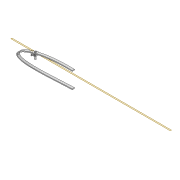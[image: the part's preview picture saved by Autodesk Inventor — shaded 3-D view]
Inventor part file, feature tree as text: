
AUTODESK INVENTOR PART (.ipt)
format: ipt  version: 2022 (Build 260153000, 153)  size: 545,280 bytes
history: native  units: mm
features: extrude x9, sketch x9, projected_geometry x7, plane x4, shell x1, fillet x1
ambient origin geometry x8: Origin, YZ Plane, XZ Plane, XY Plane, X Axis, Y Axis, Z Axis, Center Point
bodies: Solid1 (feature_tree)
feature tree (31):
  extrude  "Extrusion1"  Depth=3.0mm
  shell  "Shell1"  Thickness=5.215mm
  plane  "Work Plane3"
  sketch  "Sketch26"  dims[d69=4.1mm d70=63.6mm]
  plane  "Work Plane4"
  extrude  "Extrusion9"  Depth=63.6mm
  plane  "Work Plane5"
  extrude  "Extrusion10"  Depth=4.2mm
  extrude  "Extrusion11"  Depth=6.0mm
  extrude  "Extrusion12"  Depth=21.0mm TaperAngle=0.0deg
  plane  "Work Plane6"
  extrude  "Extrusion13"  Depth=5.0mm
  extrude  "Extrusion15"  Depth=3.0mm TaperAngle=0.0deg
  extrude  "Extrusion16"  Depth=2.0mm
  extrude  "Extrusion17"  Depth=4.0mm
  fillet  "Fillet2"  Radius=4.0mm
  sketch  "Sketch3"  dims[d0=12.0mm d1=0.0mm d2=3.0mm d68=5.215mm]
  sketch  "Sketch27"  dims[d71=12.0mm d72=4.2mm]
  projected_geometry  "Projected Loop13"
  sketch  "Sketch29"  dims[d73=63.6mm d74=6.0mm]
  sketch  "Sketch30"  dims[d75=7.0mm d76=21.0mm d77=0.0mm]
  projected_geometry  "Projected Loop14"
  sketch  "Sketch31"  dims[d78=-11.5mm d79=5.0mm]
  projected_geometry  "Projected Loop15"
  projected_geometry  "Projected Loop16"
  projected_geometry  "Projected Loop17"
  sketch  "Sketch33"  dims[d80=10.0mm d83=3.0mm d84=0.0mm]
  sketch  "Sketch34"  dims[d86=0.65mm d87=2.0mm]
  projected_geometry  "Projected Loop18"
  sketch  "Sketch35"  dims[d88=2.0mm d89=4.0mm d90=4.0mm d91=3.0mm d92=0.0mm d93=12.0mm d94=7.0mm d95=0.0mm d96=28.0mm d98=9.0mm d99=0.0mm d103=200.0mm d104=100.0mm d105=0.0mm d106=7.0mm d107=4.1mm d108=7.0mm d109=2.0mm d110=0.0mm d111=2.0mm d112=0.0mm d113=2.0mm]
  projected_geometry  "Projected Loop19"
